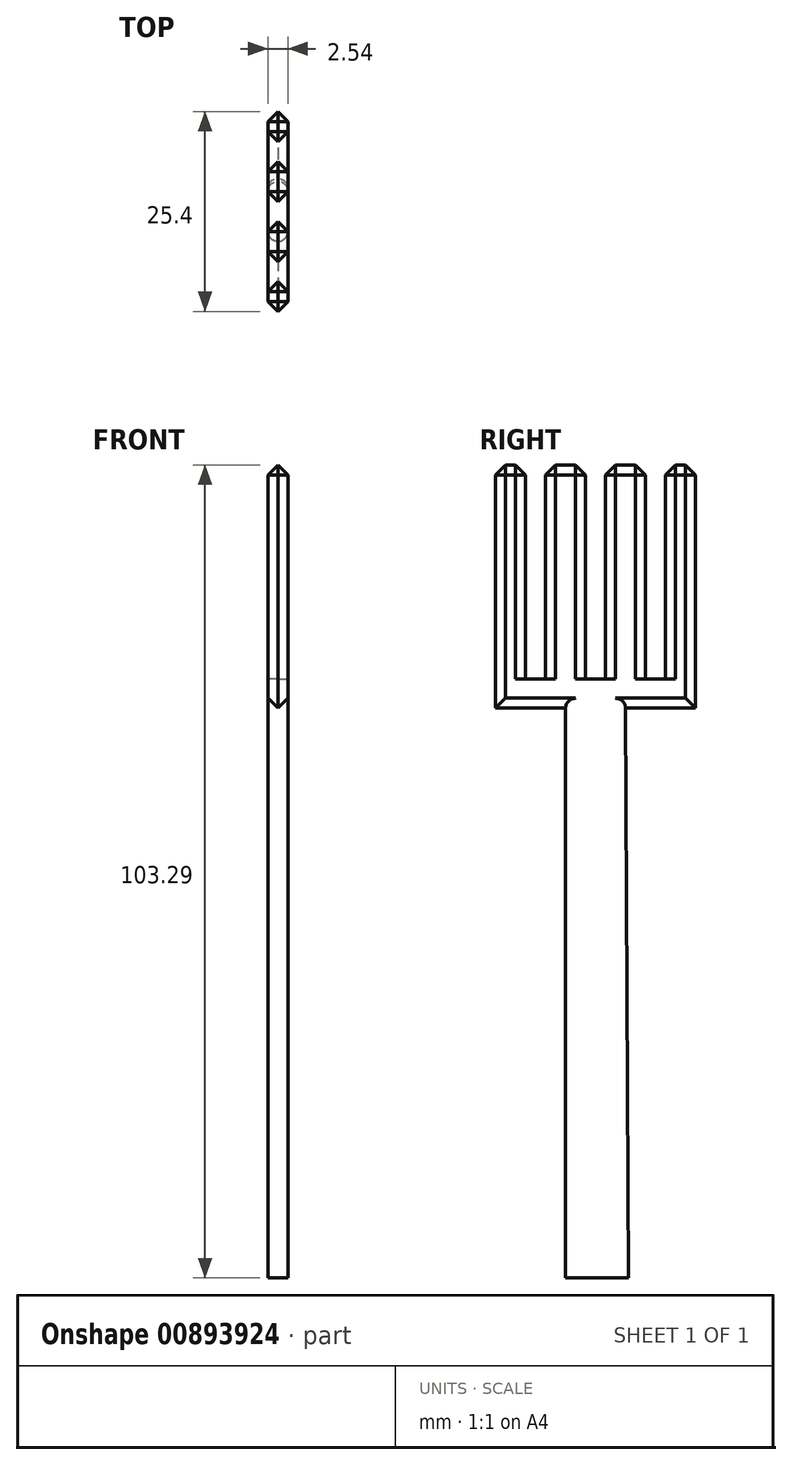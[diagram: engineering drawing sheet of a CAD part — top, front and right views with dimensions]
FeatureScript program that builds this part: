
annotation { "Feature Type Name" : "Feature", "Feature Type Description" : "" }
export const myFeature = defineFeature(function(context is Context, id is Id, definition is map)
    precondition{}
    {
        {
            var Q0;
            Q0=qCreatedBy(makeId("Right.planeOp"),FACE);
            var sketch = newSketch(context, id + "F0", { "sketchPlane" : qUnion([Q0])});
            skLineSegment(sketch, "E0", {"start": v(48.98, -55.54) * mm, "end": v(41.36, -55.54) * mm});
            skLineSegment(sketch, "E1", {"start": v(41.36, -55.54) * mm, "end": v(41.36, 16.85) * mm});
            skLineSegment(sketch, "E2", {"start": v(41.36, 16.85) * mm, "end": v(32.47, 16.85) * mm});
            skLineSegment(sketch, "E3", {"start": v(32.47, 16.85) * mm, "end": v(32.47, 47.75) * mm});
            skLineSegment(sketch, "E4", {"start": v(32.47, 47.75) * mm, "end": v(36.28, 47.75) * mm});
            skLineSegment(sketch, "E5", {"start": v(36.28, 47.75) * mm, "end": v(36.28, 20.55) * mm});
            skLineSegment(sketch, "E6", {"start": v(36.28, 20.55) * mm, "end": v(38.82, 20.55) * mm});
            skLineSegment(sketch, "E7", {"start": v(38.82, 20.55) * mm, "end": v(38.82, 47.75) * mm});
            skLineSegment(sketch, "E8", {"start": v(38.82, 47.75) * mm, "end": v(43.9, 47.75) * mm});
            skLineSegment(sketch, "E9", {"start": v(43.9, 47.75) * mm, "end": v(43.9, 20.55) * mm});
            skLineSegment(sketch, "E10", {"start": v(51.52, 20.55) * mm, "end": v(51.52, 47.75) * mm});
            skLineSegment(sketch, "E11", {"start": v(54.06, 20.55) * mm, "end": v(54.06, 47.75) * mm});
            skLineSegment(sketch, "E12", {"start": v(54.06, 47.75) * mm, "end": v(57.87, 47.75) * mm});
            skLineSegment(sketch, "E13", {"start": v(57.87, 47.75) * mm, "end": v(57.87, 20.55) * mm});
            skLineSegment(sketch, "E14", {"start": v(57.87, 20.55) * mm, "end": v(57.87, 16.85) * mm});
            skLineSegment(sketch, "E15", {"start": v(57.87, 16.85) * mm, "end": v(48.98, 16.85) * mm});
            skLineSegment(sketch, "E16", {"start": v(48.98, 16.85) * mm, "end": v(49.36, -55.54) * mm});
            skLineSegment(sketch, "E17", {"start": v(54.06, 20.55) * mm, "end": v(51.52, 20.55) * mm});
            skLineSegment(sketch, "E18", {"start": v(51.52, 47.75) * mm, "end": v(46.44, 47.75) * mm});
            skLineSegment(sketch, "E19", {"start": v(46.44, 47.75) * mm, "end": v(46.44, 20.55) * mm});
            skLineSegment(sketch, "E20", {"start": v(46.44, 20.55) * mm, "end": v(43.9, 20.55) * mm});
            skLineSegment(sketch, "E21", {"start": v(48.98, -55.54) * mm, "end": v(49.36, -55.54) * mm});
            skSolve(sketch);
        }
        {
            var Q0;
            Q0 = qSketchRegion(id + "F0", true);
            extrude(context, id + "F1", {"entities" : qUnion([Q0]), "depth" : 2.54 * mm, "offsetDistance" : 25.4 * mm});
        }
        {
            var Q0;
            Q0=makeQuery(id+"F1.opExtrude","CAP_EDGE",EDGE,{"disambiguationData":[OSD([sQuery(id+"F0.wireOp",EDGE,"E16")])],"isStart":true});
            var Q1;
            Q1=makeQuery(id+"F1.opExtrude","CAP_EDGE",EDGE,{"disambiguationData":[OSD([sQuery(id+"F0.wireOp",EDGE,"E1")])],"isStart":false});
            var Q2;
            Q2=makeQuery(id+"F1.opExtrude","CAP_EDGE",EDGE,{"disambiguationData":[OSD([sQuery(id+"F0.wireOp",EDGE,"E1")])],"isStart":true});
            var Q3;
            Q3=makeQuery(id+"F1.opExtrude","CAP_EDGE",EDGE,{"disambiguationData":[OSD([sQuery(id+"F0.wireOp",EDGE,"E16")])],"isStart":false});
            fillet(context, id + "F2", {"entities" : qUnion([Q0, Q1, Q2, Q3]), "radius" : 1.27 * mm, "tangentPropagation" : true, "allowEdgeOverflow" : false});
        }
        {
            var Q0;
            Q0=makeQuery(id+"F1.opExtrude","CAP_EDGE",EDGE,{"disambiguationData":[OSD([sQuery(id+"F0.wireOp",EDGE,"E15")])],"isStart":true});
            var Q1;
            Q1=makeQuery(id+"F1.opExtrude","CAP_EDGE",EDGE,{"disambiguationData":[OSD([sQuery(id+"F0.wireOp",EDGE,"E15")])],"isStart":false});
            var Q2;
            Q2=makeQuery(id+"F1.opExtrude","CAP_EDGE",EDGE,{"disambiguationData":[OSD([sQuery(id+"F0.wireOp",EDGE,"E2")])],"isStart":true});
            var Q3;
            Q3=makeQuery(id+"F1.opExtrude","CAP_EDGE",EDGE,{"disambiguationData":[OSD([sQuery(id+"F0.wireOp",EDGE,"E2")])],"isStart":false});
            var Q4;
            Q4=makeQuery(id+"F1.opExtrude","CAP_EDGE",EDGE,{"disambiguationData":[OSD([sQuery(id+"F0.wireOp",EDGE,"E13"),sQuery(id+"F0.wireOp",EDGE,"E14")])],"isStart":true});
            var Q5;
            Q5=makeQuery(id+"F1.opExtrude","CAP_EDGE",EDGE,{"disambiguationData":[OSD([sQuery(id+"F0.wireOp",EDGE,"E13"),sQuery(id+"F0.wireOp",EDGE,"E14")])],"isStart":false});
            var Q6;
            Q6=makeQuery(id+"F1.opExtrude","CAP_EDGE",EDGE,{"disambiguationData":[OSD([sQuery(id+"F0.wireOp",EDGE,"E11")])],"isStart":false});
            var Q7;
            Q7=makeQuery(id+"F1.opExtrude","CAP_EDGE",EDGE,{"disambiguationData":[OSD([sQuery(id+"F0.wireOp",EDGE,"E11")])],"isStart":true});
            var Q8;
            Q8=makeQuery(id+"F1.opExtrude","CAP_EDGE",EDGE,{"disambiguationData":[OSD([sQuery(id+"F0.wireOp",EDGE,"E5")])],"isStart":false});
            var Q9;
            Q9=makeQuery(id+"F1.opExtrude","CAP_EDGE",EDGE,{"disambiguationData":[OSD([sQuery(id+"F0.wireOp",EDGE,"E5")])],"isStart":true});
            var Q10;
            Q10=makeQuery(id+"F1.opExtrude","CAP_EDGE",EDGE,{"disambiguationData":[OSD([sQuery(id+"F0.wireOp",EDGE,"E9")])],"isStart":false});
            var Q11;
            Q11=makeQuery(id+"F1.opExtrude","CAP_EDGE",EDGE,{"disambiguationData":[OSD([sQuery(id+"F0.wireOp",EDGE,"E9")])],"isStart":true});
            var Q12;
            Q12=makeQuery(id+"F1.opExtrude","CAP_EDGE",EDGE,{"disambiguationData":[OSD([sQuery(id+"F0.wireOp",EDGE,"E10")])],"isStart":false});
            var Q13;
            Q13=makeQuery(id+"F1.opExtrude","CAP_EDGE",EDGE,{"disambiguationData":[OSD([sQuery(id+"F0.wireOp",EDGE,"E10")])],"isStart":true});
            var Q14;
            Q14=makeQuery(id+"F1.opExtrude","CAP_EDGE",EDGE,{"disambiguationData":[OSD([sQuery(id+"F0.wireOp",EDGE,"E3")])],"isStart":false});
            var Q15;
            Q15=makeQuery(id+"F1.opExtrude","CAP_EDGE",EDGE,{"disambiguationData":[OSD([sQuery(id+"F0.wireOp",EDGE,"E3")])],"isStart":true});
            var Q16;
            Q16=makeQuery(id+"F1.opExtrude","CAP_EDGE",EDGE,{"disambiguationData":[OSD([sQuery(id+"F0.wireOp",EDGE,"E7")])],"isStart":false});
            var Q17;
            Q17=makeQuery(id+"F1.opExtrude","CAP_EDGE",EDGE,{"disambiguationData":[OSD([sQuery(id+"F0.wireOp",EDGE,"E7")])],"isStart":true});
            var Q18;
            Q18=makeQuery(id+"F1.opExtrude","CAP_EDGE",EDGE,{"disambiguationData":[OSD([sQuery(id+"F0.wireOp",EDGE,"E19")])],"isStart":false});
            var Q19;
            Q19=makeQuery(id+"F1.opExtrude","CAP_EDGE",EDGE,{"disambiguationData":[OSD([sQuery(id+"F0.wireOp",EDGE,"E19")])],"isStart":true});
            var Q20;
            Q20=makeQuery(id+"F1.opExtrude","SWEPT_FACE",FACE,{"disambiguationData":[OSD([sQuery(id+"F0.wireOp",EDGE,"E18")])]});
            var Q21;
            Q21=makeQuery(id+"F1.opExtrude","SWEPT_FACE",FACE,{"disambiguationData":[OSD([sQuery(id+"F0.wireOp",EDGE,"E8")])]});
            var Q22;
            Q22=makeQuery(id+"F1.opExtrude","SWEPT_FACE",FACE,{"disambiguationData":[OSD([sQuery(id+"F0.wireOp",EDGE,"E4")])]});
            var Q23;
            Q23=makeQuery(id+"F1.opExtrude","SWEPT_FACE",FACE,{"disambiguationData":[OSD([sQuery(id+"F0.wireOp",EDGE,"E12")])]});
            chamfer(context, id + "F3", {"entities" : qUnion([Q0, Q1, Q2, Q3, Q4, Q5, Q6, Q7, Q8, Q9, Q10, Q11, Q12, Q13, Q14, Q15, Q16, Q17, Q18, Q19, Q20, Q21, Q22, Q23]), "width" : 1.27 * mm, "tangentPropagation" : true});
        }
    });
